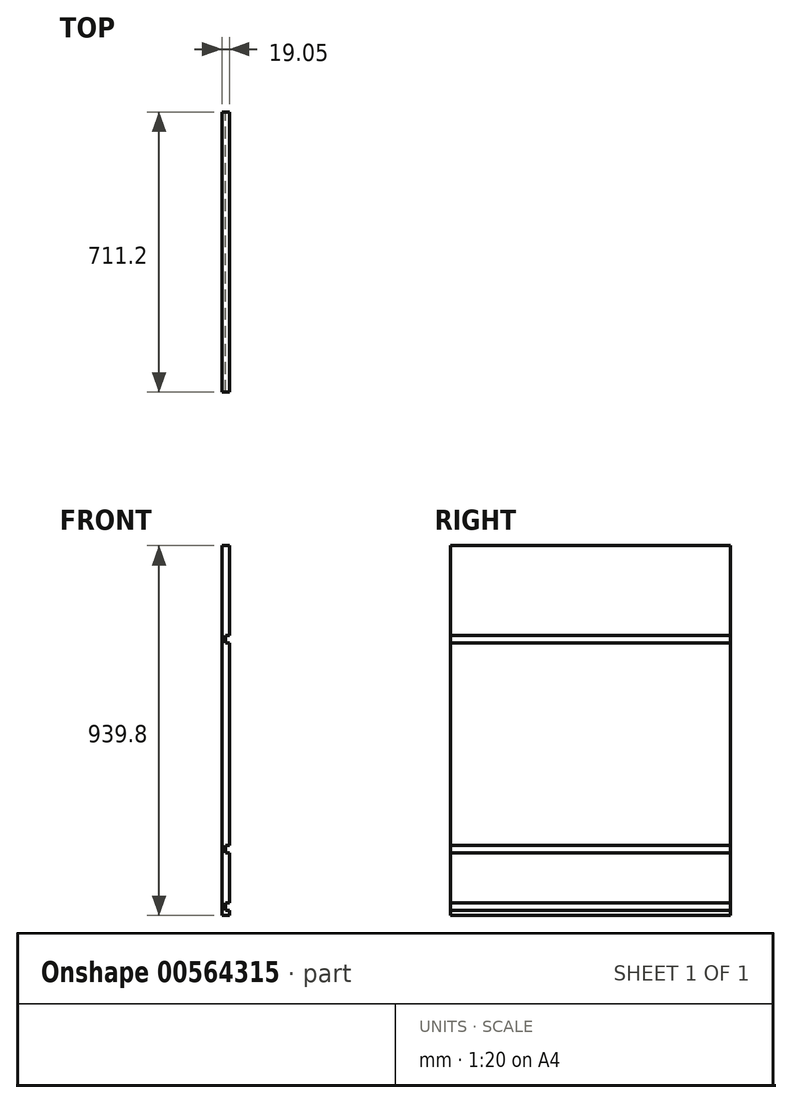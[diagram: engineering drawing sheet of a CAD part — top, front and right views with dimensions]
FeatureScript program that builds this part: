
annotation { "Feature Type Name" : "Feature", "Feature Type Description" : "" }
export const myFeature = defineFeature(function(context is Context, id is Id, definition is map)
    precondition{}
    {
        {
            var Q0;
            Q0=qCreatedBy(makeId("Front.planeOp"),FACE);
            var sketch = newSketch(context, id + "F0", { "sketchPlane" : qUnion([Q0])});
            skLineSegment(sketch, "E0.bottom", {"start": v(-13.1, 605.63) * mm, "end": v(5.95, 605.63) * mm});
            skLineSegment(sketch, "E0.top", {"start": v(-13.1, -334.17) * mm, "end": v(5.95, -334.17) * mm});
            skLineSegment(sketch, "E0.left", {"start": v(-13.1, 605.63) * mm, "end": v(-13.1, -334.17) * mm});
            skLineSegment(sketch, "E0.right", {"start": v(5.95, 605.63) * mm, "end": v(5.95, 377.03) * mm});
            skLineSegment(sketch, "E1.bottom", {"start": v(5.95, 377.03) * mm, "end": v(-3.57, 377.03) * mm});
            skLineSegment(sketch, "E1.top", {"start": v(5.95, 357.98) * mm, "end": v(-3.57, 357.98) * mm});
            skLineSegment(sketch, "E1.right", {"start": v(-3.57, 377.03) * mm, "end": v(-3.57, 357.98) * mm});
            skLineSegment(sketch, "E2.trimOffspring", {"start": v(5.95, 357.98) * mm, "end": v(5.95, -156.37) * mm});
            skLineSegment(sketch, "E3.bottom", {"start": v(5.95, -321.47) * mm, "end": v(-3.57, -321.47) * mm});
            skLineSegment(sketch, "E3.top", {"start": v(5.95, -302.42) * mm, "end": v(-3.57, -302.42) * mm});
            skLineSegment(sketch, "E3.right", {"start": v(-3.57, -321.47) * mm, "end": v(-3.57, -302.42) * mm});
            skLineSegment(sketch, "E4.trimOffspring", {"start": v(5.95, -321.47) * mm, "end": v(5.95, -334.17) * mm});
            skLineSegment(sketch, "E5.bottom", {"start": v(5.95, -175.42) * mm, "end": v(-3.57, -175.42) * mm});
            skLineSegment(sketch, "E5.top", {"start": v(5.95, -156.37) * mm, "end": v(-3.57, -156.37) * mm});
            skLineSegment(sketch, "E5.right", {"start": v(-3.57, -175.42) * mm, "end": v(-3.57, -156.37) * mm});
            skLineSegment(sketch, "E6.trimOffspring", {"start": v(5.95, -175.42) * mm, "end": v(5.95, -302.42) * mm});
            skSolve(sketch);
        }
        {
            var Q0;
            Q0 = qSketchRegion(id + "F0", true);
            extrude(context, id + "F1", {"entities" : qUnion([Q0]), "depth" : 711.2 * mm, "offsetDistance" : 25.4 * mm});
        }
    });
